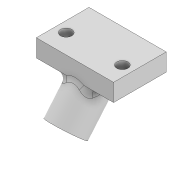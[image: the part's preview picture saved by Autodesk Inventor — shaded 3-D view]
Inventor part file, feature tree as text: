
AUTODESK INVENTOR PART (.ipt)
format: ipt  version: 2022 (Build 260153000, 153)  size: 231,936 bytes
history: native  units: mm
features: extrude x7, sketch x6, projected_geometry x3, plane x2, fillet x1
ambient origin geometry x8: Origin, YZ Plane, XZ Plane, XY Plane, X Axis, Y Axis, Z Axis, Center Point
bodies: Body1 (feature_tree)
feature tree (19):
  sketch  "Sketch6"  dims[d29=22.0mm d30=15.0mm]
  extrude  "Extrusion6"  Depth=15.0mm
  plane  "Work Plane3"
  extrude  "Extrusion7"  [1 undecoded]
  extrude  "Extrusion9"  Depth=5.0mm
  extrude  "Extrusion12"  Depth=10.0mm
  fillet  "Fillet4"  Radius=10.0mm
  plane  "Work Plane4"
  sketch  "Sketch16"  dims[d43=3.2mm d44=3.2mm]
  extrude  "Extrusion14"  Depth=3.2mm
  extrude  "Extrusion15"  Depth=10.0mm
  extrude  "Extrusion16"  Depth=10.0mm
  sketch  "Sketch7"  dims[d31=5.0mm d32=0.0mm d33=-6.981317mm]
  sketch  "Sketch9"  dims[d34=5.5mm d35=5.0mm]
  sketch  "Sketch12"  dims[d36=11.0mm d37=10.0mm d38=10.0mm d39=0.0mm]
  projected_geometry  "Projected Loop4"
  projected_geometry  "Projected Loop5"
  sketch  "Sketch17"  dims[d45=5.5mm d46=5.5mm d47=3.0mm d48=3.0mm d49=10.0mm d50=0.0mm d51=20.0mm d52=0.0mm d59=100.0mm d60=0.0mm d61=2.0mm d66=-15.0mm d67=15.0mm d68=0.0mm d69=6.0mm d70=0.0mm d71=100.0mm d72=0.0mm d12=0.5mm d13=0.872665mm d14=0.5mm d15=0.872665mm]
  projected_geometry  "Projected Loop6"
note: 1 required parameter value undecoded (feature->parameter linkage not recoverable at this tier; creation-order binding heuristic only, values carry confidence <= 0.55)
